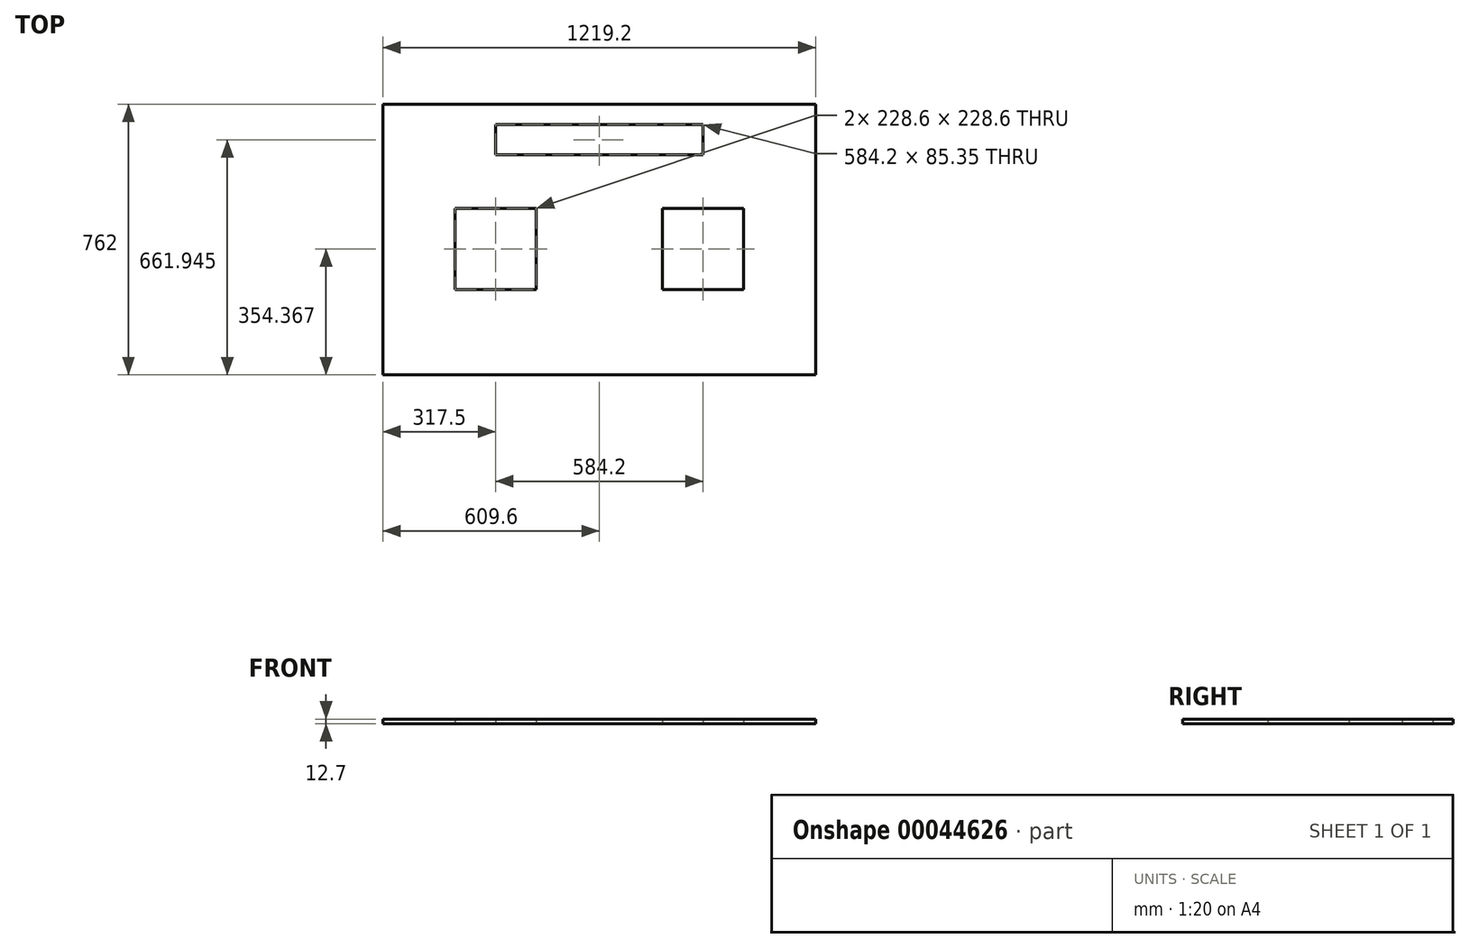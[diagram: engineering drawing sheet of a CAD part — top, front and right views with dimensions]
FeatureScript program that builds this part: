
annotation { "Feature Type Name" : "Feature", "Feature Type Description" : "" }
export const myFeature = defineFeature(function(context is Context, id is Id, definition is map)
    precondition{}
    {
        {
            var Q0;
            Q0=qCreatedBy(makeId("Top.planeOp"),FACE);
            var sketch = newSketch(context, id + "F0", { "sketchPlane" : qUnion([Q0])});
            skLineSegment(sketch, "E0.rect.bottom", {"start": v(609.6, -381) * mm, "end": v(-609.6, -381) * mm});
            skLineSegment(sketch, "E0.rect.top", {"start": v(609.6, 381) * mm, "end": v(-609.6, 381) * mm});
            skLineSegment(sketch, "E0.rect.left", {"start": v(609.6, -381) * mm, "end": v(609.6, 381) * mm});
            skLineSegment(sketch, "E0.rect.right", {"start": v(-609.6, -381) * mm, "end": v(-609.6, 381) * mm});
            skPoint(sketch, "E0.rect.middle", {"position": v(0, 0) * mm});
            skLineSegment(sketch, "E1.bottom", {"start": v(-292.1, 323.62) * mm, "end": v(292.1, 323.62) * mm});
            skLineSegment(sketch, "E1.top", {"start": v(-292.1, 238.27) * mm, "end": v(292.1, 238.27) * mm});
            skLineSegment(sketch, "E1.left", {"start": v(-292.1, 323.62) * mm, "end": v(-292.1, 238.27) * mm});
            skLineSegment(sketch, "E1.right", {"start": v(292.1, 323.62) * mm, "end": v(292.1, 238.27) * mm});
            skLineSegment(sketch, "E2.rect.bottom", {"start": v(-177.8, -140.93) * mm, "end": v(-406.4, -140.93) * mm});
            skLineSegment(sketch, "E2.rect.top", {"start": v(-177.8, 87.67) * mm, "end": v(-406.4, 87.67) * mm});
            skLineSegment(sketch, "E2.rect.left", {"start": v(-177.8, -140.93) * mm, "end": v(-177.8, 87.67) * mm});
            skLineSegment(sketch, "E2.rect.right", {"start": v(-406.4, -140.93) * mm, "end": v(-406.4, 87.67) * mm});
            skLineSegment(sketch, "E3.rect.bottom", {"start": v(177.8, -140.93) * mm, "end": v(406.4, -140.93) * mm});
            skLineSegment(sketch, "E3.rect.top", {"start": v(177.8, 87.67) * mm, "end": v(406.4, 87.67) * mm});
            skLineSegment(sketch, "E3.rect.left", {"start": v(177.8, -140.93) * mm, "end": v(177.8, 87.67) * mm});
            skLineSegment(sketch, "E3.rect.right", {"start": v(406.4, -140.93) * mm, "end": v(406.4, 87.67) * mm});
            skPoint(sketch, "E3.rect.middle", {"position": v(292.1, -26.63) * mm});
            skSolve(sketch);
        }
        {
            var Q0;
            Q0=makeQuery(id+"F0.imprint","IMPRINT",FACE,{"disambiguationData":[TD([[makeQuery(id+"F0.imprint","IMPRINT",EDGE,{"derivedFrom":sQuery(id+"F0.wireOp",EDGE,"E0.rect.bottom")}),-1.0]])]});
            extrude(context, id + "F1", {"entities" : qUnion([Q0]), "depth" : 12.7 * mm});
        }
    });
